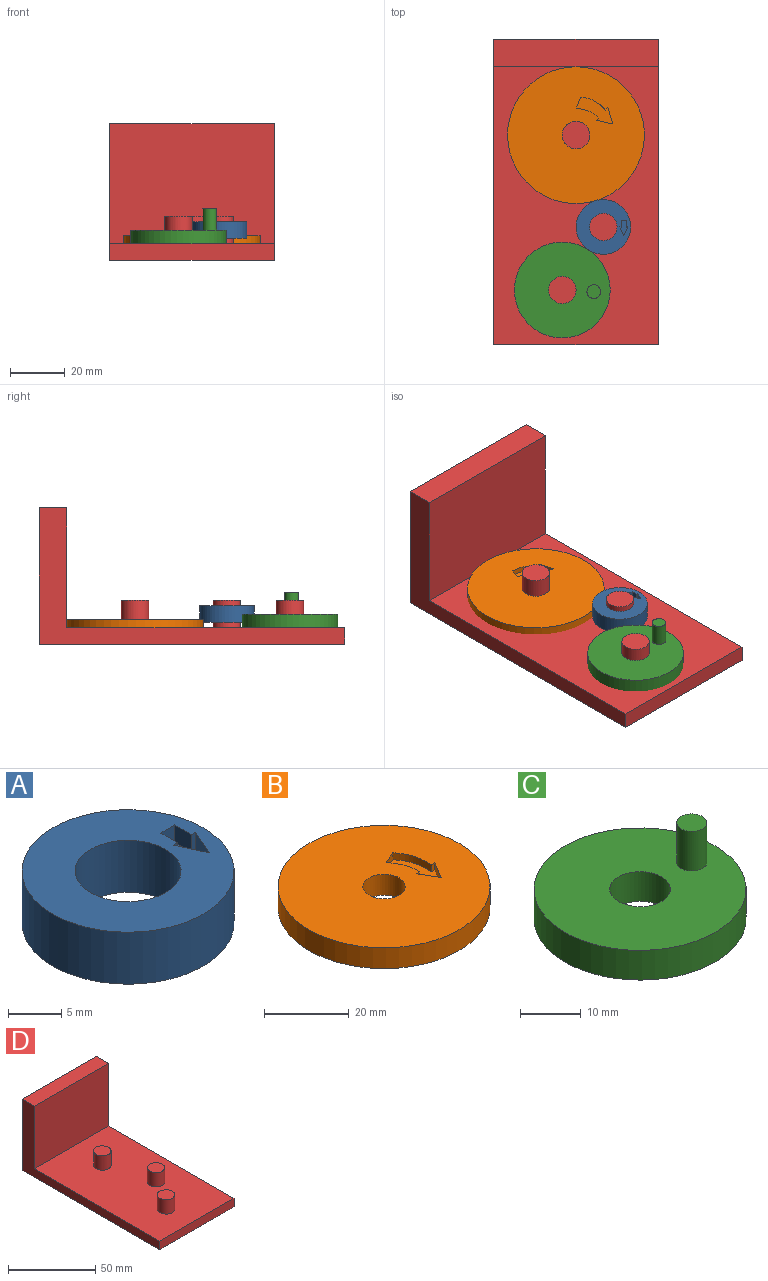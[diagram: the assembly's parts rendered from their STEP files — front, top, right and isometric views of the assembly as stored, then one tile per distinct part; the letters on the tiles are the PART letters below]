
ASSEMBLY  parts=4 mates=3
PART A: 12 faces, bbox 20x20x6 mm
  f0: plane 20x20mm, normal (0,0,1), area 226.6mm2, adj f1,f2,f4,f5,f6,f7,f8,f9
  f1: cylinder r=5mm len=10mm, axis (0,0,-1), area 188.5mm2, adj f0,f3
  f2: cylinder r=10mm len=20mm, axis (0,0,-1), area 377mm2, adj f0,f3
  f3: plane 20x20mm, normal (0,0,-1), area 235.6mm2, adj f1,f2
  f4: plane 2x1.85mm, normal (0,-1,0), area 3.7mm2, adj f0,f5,f10,f11
  f5: plane 2.22x2mm, normal (1,0,0), area 4.4mm2, adj f0,f4,f6,f11
  f6: plane 2x0.56mm, normal (0,-1,0), area 1.1mm2, adj f0,f5,f7,f11
  f7: plane 3.29x2mm, normal (0.91,0.41,0), area 7.2mm2, adj f0,f6,f8,f11
  f8: plane 3.29x2mm, normal (-0.91,0.41,0), area 7.2mm2, adj f0,f7,f9,f11
  f9: plane 2x0.56mm, normal (0,-1,0), area 1.1mm2, adj f0,f8,f10,f11
  f10: plane 2.22x2mm, normal (-1,0,0), area 4.4mm2, adj f0,f4,f9,f11
  f11: plane 5.51x2.96mm, normal (0,0,1), area 9mm2, adj f4,f5,f6,f7,f8,f9,f10
PART B: 12 faces, bbox 50x50x6 mm
  f0: plane 50x50mm, normal (0,0,1), area 1827.4mm2, adj f1,f2,f4,f5,f6,f7,f8,f9
  f1: cylinder r=5mm len=10mm, axis (0,0,-1), area 188.5mm2, adj f0,f3
  f2: cylinder r=25mm len=50mm, axis (0,0,-1), area 942.5mm2, adj f0,f3
  f3: plane 50x50mm, normal (0,0,-1), area 1885mm2, adj f1,f2
  f4: plane 5.27x3.13mm, normal (-0.86,0.51,0), area 12.3mm2, adj f0,f5,f10,f11
  f5: plane 2x1.1mm, normal (0,-1,0), area 2.2mm2, adj f0,f4,f6,f11
  f6: extruded ~9.94x3.02mm, area 21.3mm2, adj f0,f5,f7,f11
  f7: plane 3.84x2mm, normal (0.4,-0.92,0), area 8.4mm2, adj f0,f6,f8,f11
  f8: extruded ~8.28x2.81mm, area 17.9mm2, adj f0,f7,f9,f11
  f9: plane 2x1.1mm, normal (0,-1,0), area 2.2mm2, adj f0,f8,f10,f11
  f10: plane 5.27x3.13mm, normal (0.86,0.51,0), area 12.3mm2, adj f0,f4,f9,f11
  f11: plane 15.21x7.92mm, normal (0,0,1), area 57.6mm2, adj f4,f5,f6,f7,f8,f9,f10
PART C: 6 faces, bbox 35x35x14 mm
  f0: cylinder r=5mm len=10mm, axis (0,0,-1), area 188.5mm2, adj f2,f3
  f1: cylinder r=17.5mm len=35mm, axis (0,0,-1), area 659.7mm2, adj f2,f3
  f2: plane 35x35mm, normal (0,0,1), area 863.9mm2, adj f0,f1,f4
  f3: plane 35x35mm, normal (0,0,-1), area 883.6mm2, adj f0,f1
  f4: cylinder r=2.5mm len=8mm, axis (0,0,-1), area 125.7mm2, adj f2,f5
  f5: plane 5x5mm, normal (0,0,1), area 19.6mm2, adj f4
PART D: 14 faces, bbox 60x111.6x49.8 mm
  f0: plane 111.59x49.8mm, normal (-1,0,0), area 1107.5mm2, adj f1,f3,f4,f5,f6,f7
  f1: plane 60x6mm, normal (0,-1,0), area 360mm2, adj f0,f2,f4,f5
  f2: plane 111.59x49.8mm, normal (1,0,0), area 1107.5mm2, adj f1,f3,f4,f5,f6,f7
  f3: plane 60x49.8mm, normal (0,1,0), area 2988mm2, adj f0,f2,f5,f7
  f4: plane 101.59x60mm, normal (0,0,1), area 5859.8mm2, adj f0,f1,f2,f6,f8,f10,f12
  f5: plane 111.59x60mm, normal (0,0,-1), area 6695.4mm2, adj f0,f1,f2,f3
  f6: plane 60x43.8mm, normal (0,-1,0), area 2628mm2, adj f0,f2,f4,f7
  f7: plane 60x10mm, normal (0,0,1), area 600mm2, adj f0,f2,f3,f6
  f8: cylinder r=5mm len=10mm, axis (0,0,-1), area 314.2mm2, adj f4,f9
  f9: plane 10x10mm, normal (0,0,1), area 78.5mm2, adj f8
  f10: cylinder r=5mm len=10mm, axis (0,0,-1), area 314.2mm2, adj f4,f11
  f11: plane 10x10mm, normal (0,0,1), area 78.5mm2, adj f10
  f12: cylinder r=5mm len=10mm, axis (0,0,-1), area 314.2mm2, adj f4,f13
  f13: plane 10x10mm, normal (0,0,1), area 78.5mm2, adj f12
PLACE A t=(-2.31,-20.45,5.92)mm
PLACE B rot(axis=(0,0,1),46.7deg) t=(62.89,-18.2,0.92)mm
PLACE C t=(-2.31,-20.45,2.92)mm
PLACE D t=(-2.31,-20.45,3.92)mm fixed
MATE revolute D.f8 <-> B.f1  axis (0,0,-1) through (27.69,56.14,9.92)mm
MATE revolute D.f12 <-> C.f0  axis (0,0,-1) through (22.69,-0.45,14.92)mm
MATE revolute D.f10 <-> A.f1  axis (0,0,-1) through (37.69,22.6,14.92)mm
